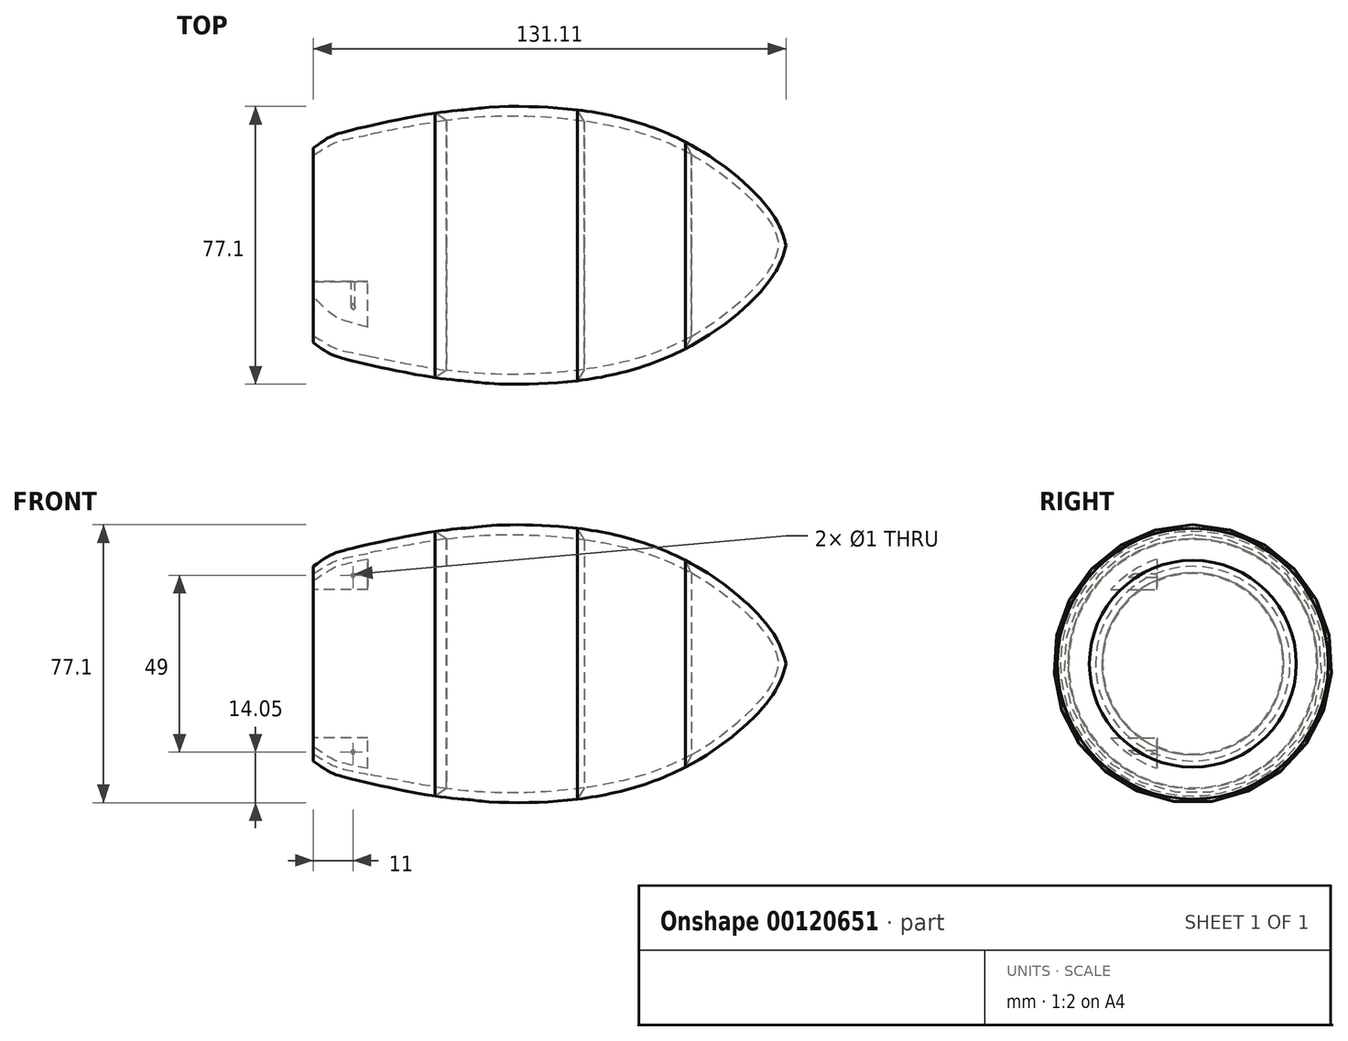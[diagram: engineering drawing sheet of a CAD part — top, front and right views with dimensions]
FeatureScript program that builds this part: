
annotation { "Feature Type Name" : "Feature", "Feature Type Description" : "" }
export const myFeature = defineFeature(function(context is Context, id is Id, definition is map)
    precondition{}
    {
        {
            var Q0;
            Q0=qCreatedBy(makeId("Front.planeOp"),FACE);
            var sketch = newSketch(context, id + "F0", { "sketchPlane" : qUnion([Q0])});
            skLineSegment(sketch, "E0.0", {"start": v(-18.15, -28) * mm, "end": v(-7.75, -28) * mm});
            skLineSegment(sketch, "E0.1", {"start": v(-29.5, -28) * mm, "end": v(-25.65, -28) * mm});
            skArc(sketch, "E0.2", {"start": v(-32.5, -25) * mm, "mid": v(-31.62, -27.12) * mm, "end": v(-29.5, -28) * mm});
            skLineSegment(sketch, "E0.3", {"start": v(-32.5, 25) * mm, "end": v(-32.5, -25) * mm});
            skCircle(sketch, "E0.4", {"center": v(-29, -24.5) * mm, "radius": 1.38 * mm});
            skArc(sketch, "E0.5", {"start": v(-29.5, 28) * mm, "mid": v(-31.62, 27.12) * mm, "end": v(-32.5, 25) * mm});
            skLineSegment(sketch, "E0.6", {"start": v(49.5, 28) * mm, "end": v(-29.5, 28) * mm});
            skCircle(sketch, "E0.7", {"center": v(-29, 24.5) * mm, "radius": 1.38 * mm});
            skCircle(sketch, "E0.8", {"center": v(29, 24.5) * mm, "radius": 1.38 * mm});
            skCircle(sketch, "E0.9", {"center": v(29, -24.5) * mm, "radius": 1.38 * mm});
            skLineSegment(sketch, "E0.10", {"start": v(24.5, -28) * mm, "end": v(49.5, -28) * mm});
            skArc(sketch, "E0.11", {"start": v(49.5, -28) * mm, "mid": v(51.37, -27.34) * mm, "end": v(52.43, -25.66) * mm});
            skLineSegment(sketch, "E0.12", {"start": v(52.5, -9.78) * mm, "end": v(52.5, -5.5) * mm});
            skLineSegment(sketch, "E0.13", {"start": v(52.5, 7.5) * mm, "end": v(52.5, 12.5) * mm});
            skArc(sketch, "E0.14", {"start": v(52.46, 25.5) * mm, "mid": v(51.44, 27.3) * mm, "end": v(49.5, 28) * mm});
            skLineSegment(sketch, "E0.15", {"start": v(6.75, -28) * mm, "end": v(17.5, -28) * mm});
            skLineSegment(sketch, "E1", {"start": v(52.46, 25.5) * mm, "end": v(52.5, 12.5) * mm, "construction": true});
            skLineSegment(sketch, "E2", {"start": v(52.5, 7.5) * mm, "end": v(52.5, -5.5) * mm, "construction": true});
            skLineSegment(sketch, "E3", {"start": v(52.5, -9.78) * mm, "end": v(52.43, -25.66) * mm, "construction": true});
            skLineSegment(sketch, "E4", {"start": v(24.5, -28) * mm, "end": v(17.5, -28) * mm, "construction": true});
            skLineSegment(sketch, "E5", {"start": v(6.75, -28) * mm, "end": v(-7.75, -28) * mm, "construction": true});
            skLineSegment(sketch, "E6", {"start": v(-18.15, -28) * mm, "end": v(-25.65, -28) * mm, "construction": true});
            skLineSegment(sketch, "E7", {"start": v(-29, 24.5) * mm, "end": v(29, -24.5) * mm, "construction": true});
            skLineSegment(sketch, "E8", {"start": v(29, 24.5) * mm, "end": v(-29, -24.5) * mm, "construction": true});
            skLineSegment(sketch, "E9", {"start": v(-29, 24.5) * mm, "end": v(-29, -24.5) * mm, "construction": true});
            skLineSegment(sketch, "E10", {"start": v(-29, -24.5) * mm, "end": v(29, -24.5) * mm, "construction": true});
            skLineSegment(sketch, "E11", {"start": v(29, -24.5) * mm, "end": v(29, 24.5) * mm, "construction": true});
            skLineSegment(sketch, "E12", {"start": v(29, 24.5) * mm, "end": v(-29, 24.5) * mm, "construction": true});
            skPoint(sketch, "E13", {"position": v(0, 0) * mm});
            skLineSegment(sketch, "E14", {"start": v(-90.89, 0) * mm, "end": v(89.11, 0) * mm});
            skFitSpline(sketch, "E15", {"points": [v(-90.89, 0) * mm, v(-90.89, -38.26) * mm], "startDerivative": vector(0, -38.26) * mm, "endDerivative": vector(0, -38.26) * mm});
            skPoint(sketch, "E16", {"position": v(-90.89, -36.26) * mm});
            skLineSegment(sketch, "E17", {"start": v(-90.89, -36.26) * mm, "end": v(-90.89, -38.26) * mm});
            skLineSegment(sketch, "E18", {"start": v(87.11, 0) * mm, "end": v(89.11, 0) * mm});
            skLineSegment(sketch, "E19", {"start": v(0, 0) * mm, "end": v(-102.3, 0) * mm, "construction": true});
            skCircle(sketch, "E20", {"center": v(-90.89, 0) * mm, "radius": 22.5 * mm});
            skLineSegment(sketch, "E21", {"start": v(-40, 0) * mm, "end": v(-40, -25) * mm, "construction": true});
            skLineSegment(sketch, "E22", {"start": v(-40, -25) * mm, "end": v(-40, -27) * mm});
            skFitSpline(sketch, "E23", {"points": [v(-40, -25) * mm, v(-35.35, -27.83) * mm, v(-32.76, -28.94) * mm, v(-25.35, -30.57) * mm, v(-7.04, -34.06) * mm, v(10.15, -35.76) * mm, v(32.9, -34.72) * mm, v(62.17, -26.65) * mm, v(84.25, -9.83) * mm, v(89.11, 0) * mm], "startDerivative": vector(74.31, -46.83) * mm, "endDerivative": vector(19.14, 115.16) * mm});
            skFitSpline(sketch, "E24", {"points": [v(-40, -27) * mm, v(-35.64, -29.94) * mm, v(-32.19, -31.27) * mm, v(-23.83, -33.31) * mm, v(-6.2, -36.72) * mm, v(3, -37.72) * mm, v(10.2, -38.39) * mm, v(33.2, -37.58) * mm, v(63.23, -28.69) * mm, v(85.38, -11.4) * mm, v(91.11, 0) * mm], "startDerivative": vector(71.84, -52.72) * mm, "endDerivative": vector(28.66, 120.89) * mm});
            skLineSegment(sketch, "E25", {"start": v(89.11, 0) * mm, "end": v(91.11, 0) * mm});
            skLineSegment(sketch, "E26", {"start": v(63.23, -28.69) * mm, "end": v(64.83, -25.24) * mm});
            skLineSegment(sketch, "E27", {"start": v(33.2, -37.58) * mm, "end": v(35.18, -34.43) * mm});
            skLineSegment(sketch, "E28", {"start": v(-6.2, -36.72) * mm, "end": v(-3.05, -34.65) * mm});
            skLineSegment(sketch, "E29", {"start": v(-24.86, -30.67) * mm, "end": v(-24.86, -20.6) * mm});
            skLineSegment(sketch, "E30", {"start": v(-24.86, -20.6) * mm, "end": v(-40, -20.6) * mm});
            skLineSegment(sketch, "E31", {"start": v(-40, -20.6) * mm, "end": v(-40, -25) * mm});
            skCircle(sketch, "E32", {"center": v(-29, -24.5) * mm, "radius": 0.5 * mm});
            skSolve(sketch);
        }
        {
            var Q0;
            Q0=qCreatedBy(makeId("Front.planeOp"),FACE);
            cPlane(context, id + "F1", {"entities" : qUnion([Q0]), "cplaneType" : CPlaneType.OFFSET, "offset" : 10 * mm, "width" : 150 * mm, "height" : 150 * mm});
        }
        {
            var Q0;
            Q0=qCreatedBy(id+"F1.planeOp",FACE);
            var sketch = newSketch(context, id + "F2", { "sketchPlane" : qUnion([Q0])});
            skLineSegment(sketch, "E33.0", {"start": v(-24.86, -20.6) * mm, "end": v(-40, -20.6) * mm});
            skLineSegment(sketch, "E34.0", {"start": v(-24.86, -30.67) * mm, "end": v(-24.86, -20.6) * mm});
            skFitSpline(sketch, "E35.0", {"points": [v(-40, -25) * mm, v(-38.3, -26.07) * mm, v(-35.39, -27.9) * mm, v(-32.64, -29.15) * mm, v(-24.69, -30.67) * mm, v(-6.54, -34.45) * mm, v(10.26, -36.2) * mm, v(33.54, -35.44) * mm, v(62.46, -29.34) * mm, v(84.95, -10.82) * mm, v(88.5, -3.73) * mm, v(89.11, 0) * mm]});
            skLineSegment(sketch, "E36.0", {"start": v(-40, -20.6) * mm, "end": v(-40, -25) * mm});
            skCircle(sketch, "E37.0", {"center": v(-29, -24.5) * mm, "radius": 0.5 * mm});
            skLineSegment(sketch, "E38.MirrorCS", {"start": v(-24.86, 20.6) * mm, "end": v(-40, 20.6) * mm});
            skLineSegment(sketch, "E39.MirrorCS", {"start": v(-24.86, 30.67) * mm, "end": v(-24.86, 20.6) * mm});
            skFitSpline(sketch, "E40.MirrorCS", {"points": [v(-40, 25) * mm, v(-38.3, 26.07) * mm, v(-35.39, 27.9) * mm, v(-32.64, 29.15) * mm, v(-24.69, 30.67) * mm, v(-6.54, 34.45) * mm, v(10.26, 36.2) * mm, v(33.54, 35.44) * mm, v(62.46, 29.34) * mm, v(84.95, 10.82) * mm, v(88.5, 3.73) * mm, v(89.11, 0) * mm]});
            skLineSegment(sketch, "E41.MirrorCS", {"start": v(-40, 20.6) * mm, "end": v(-40, 25) * mm});
            skCircle(sketch, "E42.MirrorC", {"center": v(-29, 24.5) * mm, "radius": 0.5 * mm});
            skSolve(sketch);
        }
        {
            var Q0;
            {var subQ0=sQuery(id+"F0.wireOp",EDGE,"E22");Q0=makeQuery(id+"F0.imprint","IMPRINT",FACE,{"disambiguationData":[TD([[makeQuery(id+"F0.imprint","IMPRINT",EDGE,{"derivedFrom":subQ0}),1.0]])]});}
            var Q1;
            Q1=sQuery(id+"F0.wireOp",EDGE,"E14");
            revolve(context, id + "F3", {"entities" : qUnion([Q0]), "axis" : qUnion([Q1]), "revolveType" : RevolveType.FULL});
        }
        {
            var Q0;
            {var subQ0=sQuery(id+"F0.wireOp",EDGE,"E27");Q0=makeQuery(id+"F0.imprint","IMPRINT",FACE,{"disambiguationData":[TD([[makeQuery(id+"F0.imprint","IMPRINT",EDGE,{"derivedFrom":subQ0}),1.0]])]});}
            var Q1;
            Q1=sQuery(id+"F0.wireOp",EDGE,"E14");
            revolve(context, id + "F4", {"entities" : qUnion([Q0]), "axis" : qUnion([Q1]), "revolveType" : RevolveType.FULL});
        }
        {
            var Q0;
            {var subQ0=sQuery(id+"F0.wireOp",EDGE,"E26");Q0=makeQuery(id+"F0.imprint","IMPRINT",FACE,{"disambiguationData":[TD([[makeQuery(id+"F0.imprint","IMPRINT",EDGE,{"derivedFrom":subQ0}),1.0]])]});}
            var Q1;
            Q1=sQuery(id+"F0.wireOp",EDGE,"E14");
            revolve(context, id + "F5", {"entities" : qUnion([Q0]), "axis" : qUnion([Q1]), "revolveType" : RevolveType.FULL});
        }
        {
            var Q0;
            {var subQ0=sQuery(id+"F0.wireOp",EDGE,"E25");Q0=makeQuery(id+"F0.imprint","IMPRINT",FACE,{"disambiguationData":[TD([[makeQuery(id+"F0.imprint","IMPRINT",EDGE,{"derivedFrom":subQ0}),-1.0]])]});}
            var Q1;
            Q1=sQuery(id+"F0.wireOp",EDGE,"E14");
            revolve(context, id + "F6", {"entities" : qUnion([Q0]), "axis" : qUnion([Q1]), "revolveType" : RevolveType.FULL});
        }
        {
            var Q0;
            Q0=makeQuery(id+"F2.imprint","IMPRINT",FACE,{"disambiguationData":[TD([[makeQuery(id+"F2.imprint","IMPRINT",EDGE,{"derivedFrom":sQuery(id+"F2.wireOp",EDGE,"E33.0")}),1.0]])]});
            var Q1;
            Q1=makeQuery(id+"F2.imprint","IMPRINT",FACE,{"disambiguationData":[TD([[makeQuery(id+"F2.imprint","IMPRINT",EDGE,{"derivedFrom":sQuery(id+"F2.wireOp",EDGE,"E38.MirrorCS")}),-1.0]])]});
            var Q2;
            Q2=makeQuery(id+"F3.opRevolve","SWEPT_FACE",FACE,{"disambiguationData":[OSD([sQuery(id+"F0.wireOp",EDGE,"E23")])]});
            extrude(context, id + "F7", {"entities" : qUnion([Q0, Q1]), "operationType" : NewBodyOperationType.ADD, "endBound" : BoundingType.UP_TO_SURFACE, "endBoundEntityFace" : qUnion([Q2]), "depth" : 25 * mm});
        }
    });
